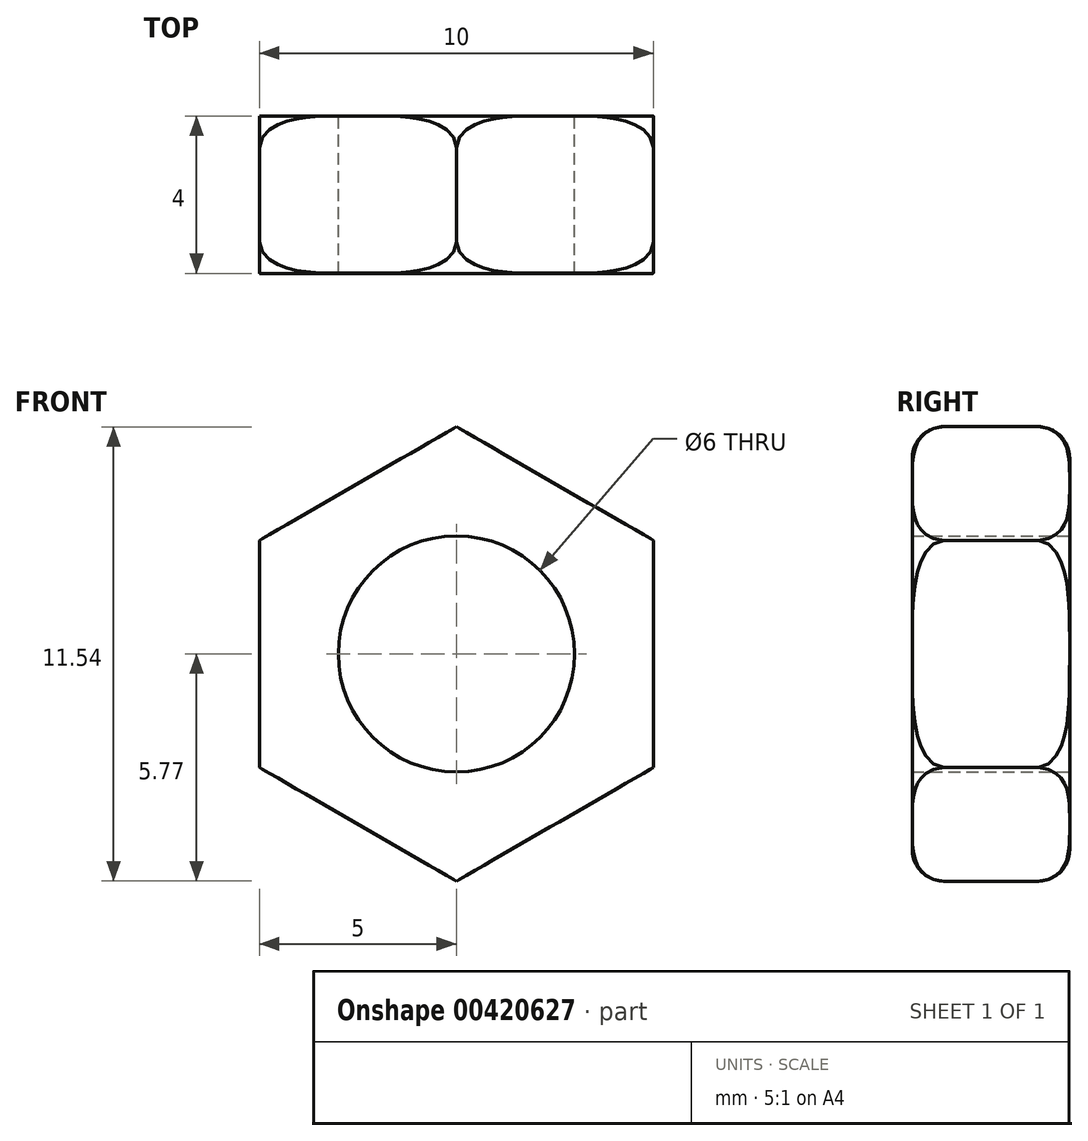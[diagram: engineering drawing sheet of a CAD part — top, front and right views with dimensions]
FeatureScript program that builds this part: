
annotation { "Feature Type Name" : "Feature", "Feature Type Description" : "" }
export const myFeature = defineFeature(function(context is Context, id is Id, definition is map)
    precondition{}
    {
        {
            var Q0;
            Q0=qCreatedBy(makeId("Front.planeOp"),FACE);
            var sketch = newSketch(context, id + "F0", { "sketchPlane" : qUnion([Q0])});
            skCircle(sketch, "E0", {"center": v(0, 0) * mm, "radius": 5.77 * mm});
            skCircle(sketch, "E1", {"center": v(0, 0) * mm, "radius": 3 * mm});
            skCircle(sketch, "E2.cCircle", {"center": v(0, 0) * mm, "radius": 5 * mm, "construction": true});
            skLineSegment(sketch, "E2.0", {"start": v(-5.77, 0) * mm, "end": v(-2.89, 5) * mm, "construction": true});
            skLineSegment(sketch, "E2.1", {"start": v(-2.89, 5) * mm, "end": v(2.89, 5) * mm, "construction": true});
            skLineSegment(sketch, "E2.2", {"start": v(2.89, 5) * mm, "end": v(5.77, 0) * mm, "construction": true});
            skLineSegment(sketch, "E2.3", {"start": v(5.77, 0) * mm, "end": v(2.89, -5) * mm, "construction": true});
            skLineSegment(sketch, "E2.4", {"start": v(2.89, -5) * mm, "end": v(-2.89, -5) * mm, "construction": true});
            skLineSegment(sketch, "E2.5", {"start": v(-2.89, -5) * mm, "end": v(-5.77, 0) * mm, "construction": true});
            skPoint(sketch, "E2.0.midPoint", {"position": v(-4.33, 2.5) * mm});
            skSolve(sketch);
        }
        {
            var Q0;
            Q0=qSketchRegion(id+"F0",true);
            extrude(context, id + "F1", {"entities" : qUnion([Q0]), "depth" : 4 * mm, "offsetDistance" : 25 * mm, "symmetric" : true});
        }
        {
            var Q0;
            Q0=makeQuery(id+"F1.opExtrude","CAP_FACE",FACE,{"disambiguationData":[OSD([sQuery(id+"F0.wireOp",EDGE,"E0"),sQuery(id+"F0.wireOp",EDGE,"E1")])],"isStart":false});
            var sketch = newSketch(context, id + "F2", { "sketchPlane" : qUnion([Q0])});
            skCircle(sketch, "E3.cCircle", {"center": v(0, 0) * mm, "radius": 5 * mm, "construction": true});
            skLineSegment(sketch, "E3.0", {"start": v(-5, -2.89) * mm, "end": v(-5, 2.89) * mm});
            skLineSegment(sketch, "E3.1", {"start": v(-5, 2.89) * mm, "end": v(0, 5.77) * mm});
            skLineSegment(sketch, "E3.2", {"start": v(0, 5.77) * mm, "end": v(5, 2.89) * mm});
            skLineSegment(sketch, "E3.3", {"start": v(5, 2.89) * mm, "end": v(5, -2.89) * mm});
            skLineSegment(sketch, "E3.4", {"start": v(5, -2.89) * mm, "end": v(0, -5.77) * mm});
            skLineSegment(sketch, "E3.5", {"start": v(0, -5.77) * mm, "end": v(-5, -2.89) * mm});
            skPoint(sketch, "E3.0.midPoint", {"position": v(-5, 0) * mm});
            skCircle(sketch, "E4", {"center": v(0, 0) * mm, "radius": 6 * mm});
            skSolve(sketch);
        }
        {
            var Q0;
            Q0=makeQuery(id+"F1.opExtrude","CAP_EDGE",EDGE,{"disambiguationData":[OSD([sQuery(id+"F0.wireOp",EDGE,"E0")])],"isStart":false});
            var Q1;
            Q1=makeQuery(id+"F1.opExtrude","CAP_EDGE",EDGE,{"disambiguationData":[OSD([sQuery(id+"F0.wireOp",EDGE,"E0")])],"isStart":true});
            fillet(context, id + "F3", {"entities" : qUnion([Q0, Q1]), "radius" : 0.8 * mm, "tangentPropagation" : true, "allowEdgeOverflow" : false});
        }
        {
            var Q0;
            Q0=qSketchRegion(id+"F2",true);
            extrude(context, id + "F4", {"entities" : qUnion([Q0]), "operationType" : NewBodyOperationType.REMOVE, "endBound" : BoundingType.THROUGH_ALL, "oppositeDirection" : true, "depth" : 25 * mm});
        }
    });
